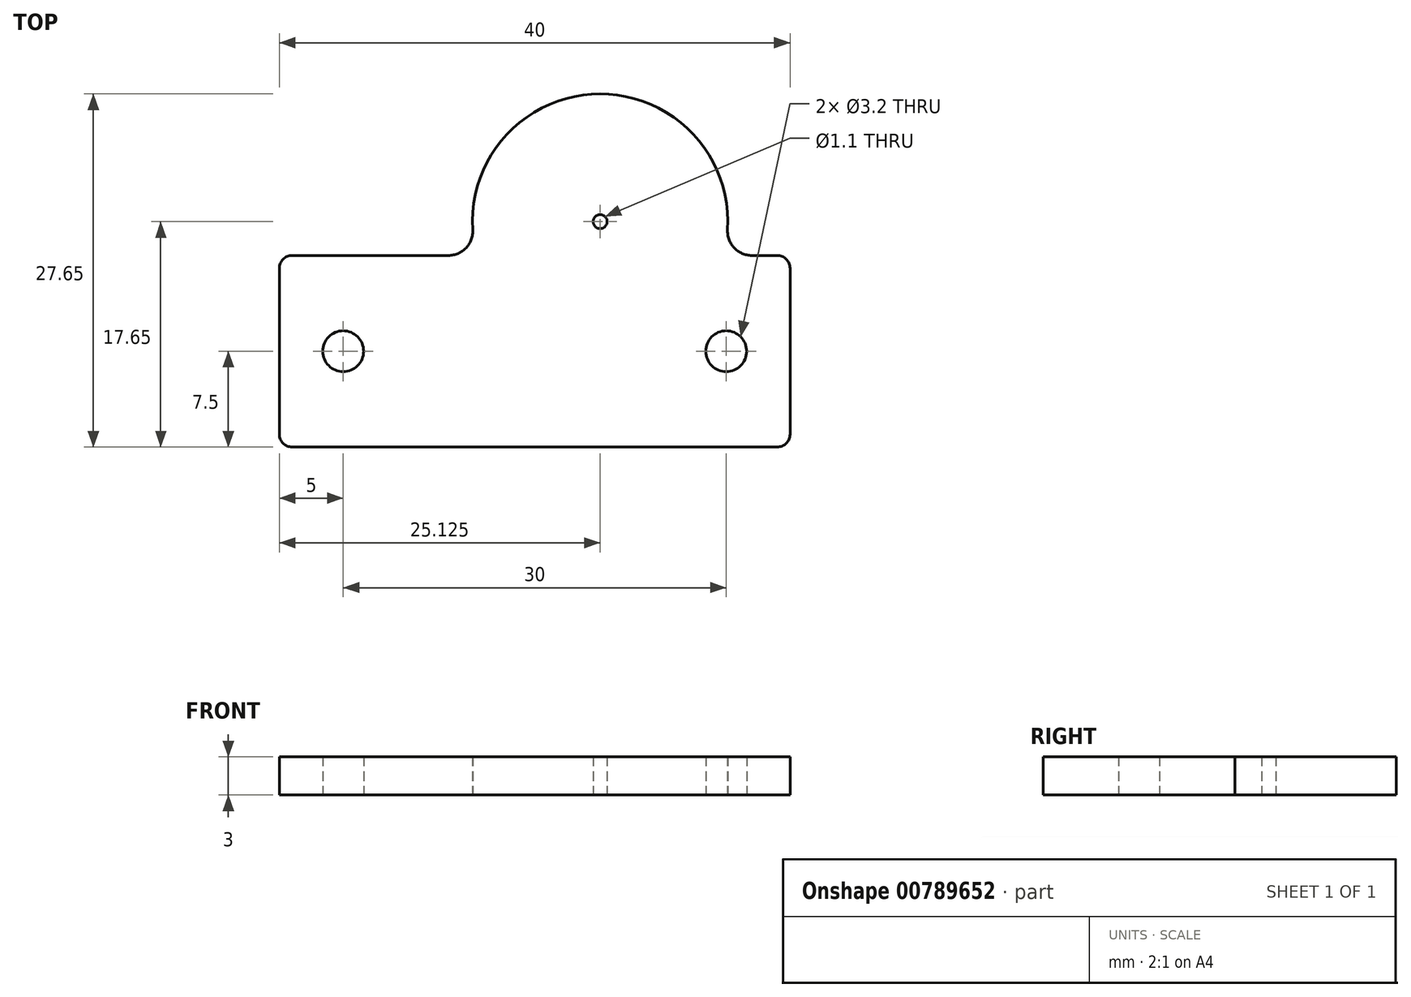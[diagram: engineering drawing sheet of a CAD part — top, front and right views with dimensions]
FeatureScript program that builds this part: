
annotation { "Feature Type Name" : "Feature", "Feature Type Description" : "" }
export const myFeature = defineFeature(function(context is Context, id is Id, definition is map)
    precondition{}
    {
        {
            var Q0;
            Q0=qCreatedBy(makeId("Top.planeOp"),FACE);
            var sketch = newSketch(context, id + "F0", { "sketchPlane" : qUnion([Q0])});
            skLineSegment(sketch, "E0", {"start": v(0, 0) * mm, "end": v(-20, 0) * mm, "construction": true});
            skLineSegment(sketch, "E1", {"start": v(0, 0) * mm, "end": v(0, 11.6) * mm, "construction": true});
            skLineSegment(sketch, "E2.MirrorCS", {"start": v(20, 7.5) * mm, "end": v(17, 7.5) * mm});
            skLineSegment(sketch, "E3.MirrorCS", {"start": v(20, -7.5) * mm, "end": v(-20, -7.5) * mm});
            skCircle(sketch, "E4", {"center": v(-15, 0) * mm, "radius": 1.6 * mm});
            skCircle(sketch, "E5.MirrorC", {"center": v(15, 0) * mm, "radius": 1.6 * mm});
            skCircle(sketch, "E6", {"center": v(5.13, 10.15) * mm, "radius": 0.55 * mm});
            skPoint(sketch, "E7.visualSharp", {"position": v(4.24, 7.5) * mm});
            skLineSegment(sketch, "E8", {"start": v(-20, 7.5) * mm, "end": v(-6.75, 7.5) * mm});
            skArc(sketch, "E9", {"start": v(15.1, 9.52) * mm, "mid": v(5.13, 20.15) * mm, "end": v(-4.86, 9.52) * mm});
            skPoint(sketch, "E10.visualSharp", {"position": v(-1.05, 7.5) * mm});
            skArc(sketch, "E10.filletArc", {"start": v(-6.75, 7.5) * mm, "mid": v(-5.37, 8.1) * mm, "end": v(-4.86, 9.52) * mm});
            skPoint(sketch, "E11.visualSharp", {"position": v(13.56, 7.5) * mm});
            skArc(sketch, "E11.filletArc", {"start": v(15.1, 9.52) * mm, "mid": v(15.62, 8.1) * mm, "end": v(17, 7.5) * mm});
            skLineSegment(sketch, "E12", {"start": v(-4.86, 9.52) * mm, "end": v(15.1, 9.52) * mm, "construction": true});
            skLineSegment(sketch, "E13.trimOffspring", {"start": v(-20, 7.5) * mm, "end": v(-20, 0) * mm});
            skLineSegment(sketch, "E14.trimOffspring", {"start": v(-20, -7.5) * mm, "end": v(-20, 0) * mm});
            skLineSegment(sketch, "E15.trimOffspring", {"start": v(20, -7.5) * mm, "end": v(20, 0) * mm});
            skLineSegment(sketch, "E16.trimOffspring", {"start": v(20, 7.5) * mm, "end": v(20, 0) * mm});
            skCircle(sketch, "E17", {"center": v(15, 0) * mm, "radius": 3 * mm, "construction": true});
            skCircle(sketch, "E18", {"center": v(-15, 0) * mm, "radius": 3 * mm, "construction": true});
            skSolve(sketch);
        }
        {
            var Q0;
            Q0=qSketchRegion(id+"F0",true);
            extrude(context, id + "F1", {"entities" : qUnion([Q0]), "depth" : 3 * mm, "offsetDistance" : 25 * mm});
        }
        {
            var Q0;
            Q0=makeQuery(id+"F1.opExtrude","SWEPT_EDGE",EDGE,{"disambiguationData":[OSD([sQuery(id+"F0.wireOp",EDGE,"E3.MirrorCS"),sQuery(id+"F0.wireOp",EDGE,"E15.trimOffspring")])]});
            var Q1;
            Q1=makeQuery(id+"F1.opExtrude","SWEPT_EDGE",EDGE,{"disambiguationData":[OSD([sQuery(id+"F0.wireOp",EDGE,"E2.MirrorCS"),sQuery(id+"F0.wireOp",EDGE,"E16.trimOffspring")])]});
            var Q2;
            Q2=makeQuery(id+"F1.opExtrude","SWEPT_EDGE",EDGE,{"disambiguationData":[OSD([sQuery(id+"F0.wireOp",EDGE,"E3.MirrorCS"),sQuery(id+"F0.wireOp",EDGE,"E14.trimOffspring")])]});
            var Q3;
            Q3=makeQuery(id+"F1.opExtrude","SWEPT_EDGE",EDGE,{"disambiguationData":[OSD([sQuery(id+"F0.wireOp",EDGE,"E8"),sQuery(id+"F0.wireOp",EDGE,"E13.trimOffspring")])]});
            fillet(context, id + "F2", {"entities" : qUnion([Q0, Q1, Q2, Q3]), "radius" : 1 * mm, "tangentPropagation" : true, "allowEdgeOverflow" : false});
        }
    });
